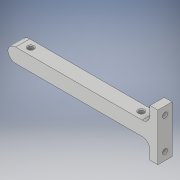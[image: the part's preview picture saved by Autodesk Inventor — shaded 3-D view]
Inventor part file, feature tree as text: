
AUTODESK INVENTOR PART (.ipt)
format: ipt  version: 2019 (Build 230136000, 136)  size: 180,736 bytes
history: native  units: mm
features: fillet x4, extrude x2, sketch x2
ambient origin geometry x8: Origin, YZ Plane, XZ Plane, XY Plane, X Axis, Y Axis, Z Axis, Center Point
bodies: Solid1 (feature_tree)
feature tree (8):
  extrude  "Extrusion1"  Depth=90.0mm
  extrude  "Extrusion2"  Depth=0.5mm
  fillet  "Fillet1"  Radius=3.2mm
  fillet  "Fillet2"  Radius=3.2mm
  fillet  "Fillet3"  Radius=90.0mm
  fillet  "Fillet4"  Radius=9.0mm
  sketch  "Sketch1"  dims[d0=70.0mm d1=90.0mm]
  sketch  "Sketch2"  dims[d2=3.2mm d3=3.2mm d4=3.2mm d5=3.2mm d6=90.0mm d7=9.0mm d8=9.0mm d9=0.0mm d10=9.0mm d11=30.0mm d12=10.0mm d13=10.0mm d14=3.2mm d15=3.2mm d16=5.0mm d17=0.0mm d18=5.0mm d19=5.0mm d20=1.0mm d21=0.5mm]
